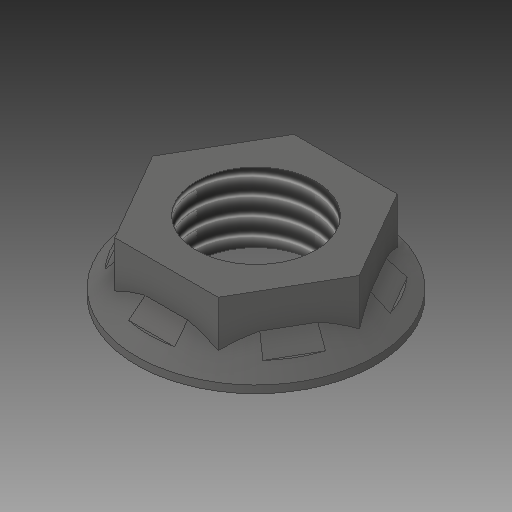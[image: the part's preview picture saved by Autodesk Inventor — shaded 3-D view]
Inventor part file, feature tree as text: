
AUTODESK INVENTOR PART (.ipt)
format: ipt  version: 2019 (Build 230136000, 136)  size: 165,376 bytes
history: native  units: mm
features: extrude x3, sketch x3, chamfer x2, thread x1
ambient origin geometry x8: Origin, YZ Plane, XZ Plane, XY Plane, X Axis, Y Axis, Z Axis, Center Point
bodies: Solid1 (feature_tree)
feature tree (9):
  extrude  "Extrusion1"  Depth=18.0mm
  extrude  "Extrusion2"  Depth=5.0mm TaperAngle=0.0deg
  chamfer  "Chamfer1"  Distance=1.25mm Angle=45.0deg
  extrude  "Extrusion3"  Depth=5.0mm TaperAngle=0.0deg
  chamfer  "Chamfer2"  Distance=1.5mm Angle=45.0deg
  thread  "Thread1"  [1 undecoded]
  sketch  "Sketch2"  dims[d0=2.0mm d1=0.0mm d2=18.0mm]
  sketch  "Sketch3"  dims[d3=24.0mm d4=5.0mm d5=0.0mm d6=1.25mm d7=2.0mm d8=45.0deg]
  sketch  "Sketch4"  dims[d9=12.0mm d10=5.0mm d11=0.0mm d12=1.5mm d13=2.0mm d14=45.0deg d15=10.0mm d16=0.0mm]
note: 1 required parameter value undecoded (feature->parameter linkage not recoverable at this tier; creation-order binding heuristic only, values carry confidence <= 0.55)
